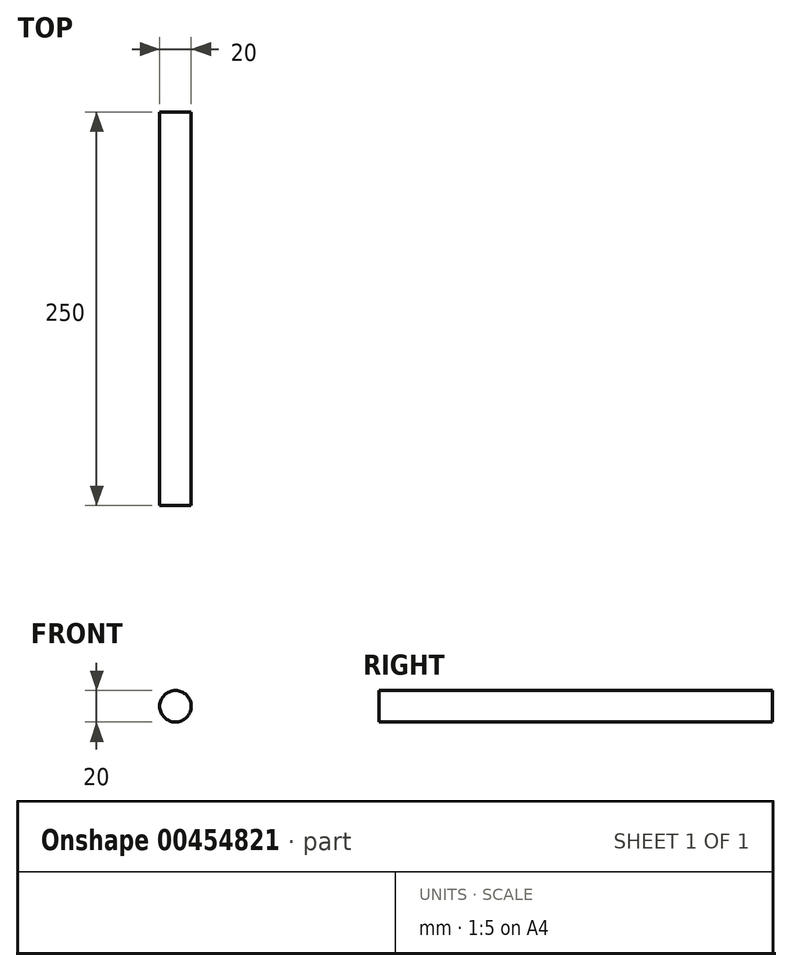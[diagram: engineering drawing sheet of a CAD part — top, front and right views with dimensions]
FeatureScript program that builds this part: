
annotation { "Feature Type Name" : "Feature", "Feature Type Description" : "" }
export const myFeature = defineFeature(function(context is Context, id is Id, definition is map)
    precondition{}
    {
        {
            var Q0;
            Q0=qCreatedBy(makeId("Front.planeOp"),FACE);
            var sketch = newSketch(context, id + "F0", { "sketchPlane" : qUnion([Q0])});
            skCircle(sketch, "E0", {"center": v(0, 0) * mm, "radius": 10 * mm});
            skSolve(sketch);
        }
        {
            var Q0;
            Q0 = qSketchRegion(id + "F0", true);
            extrude(context, id + "F1", {"entities" : qUnion([Q0]), "depth" : 250 * mm});
        }
    });
